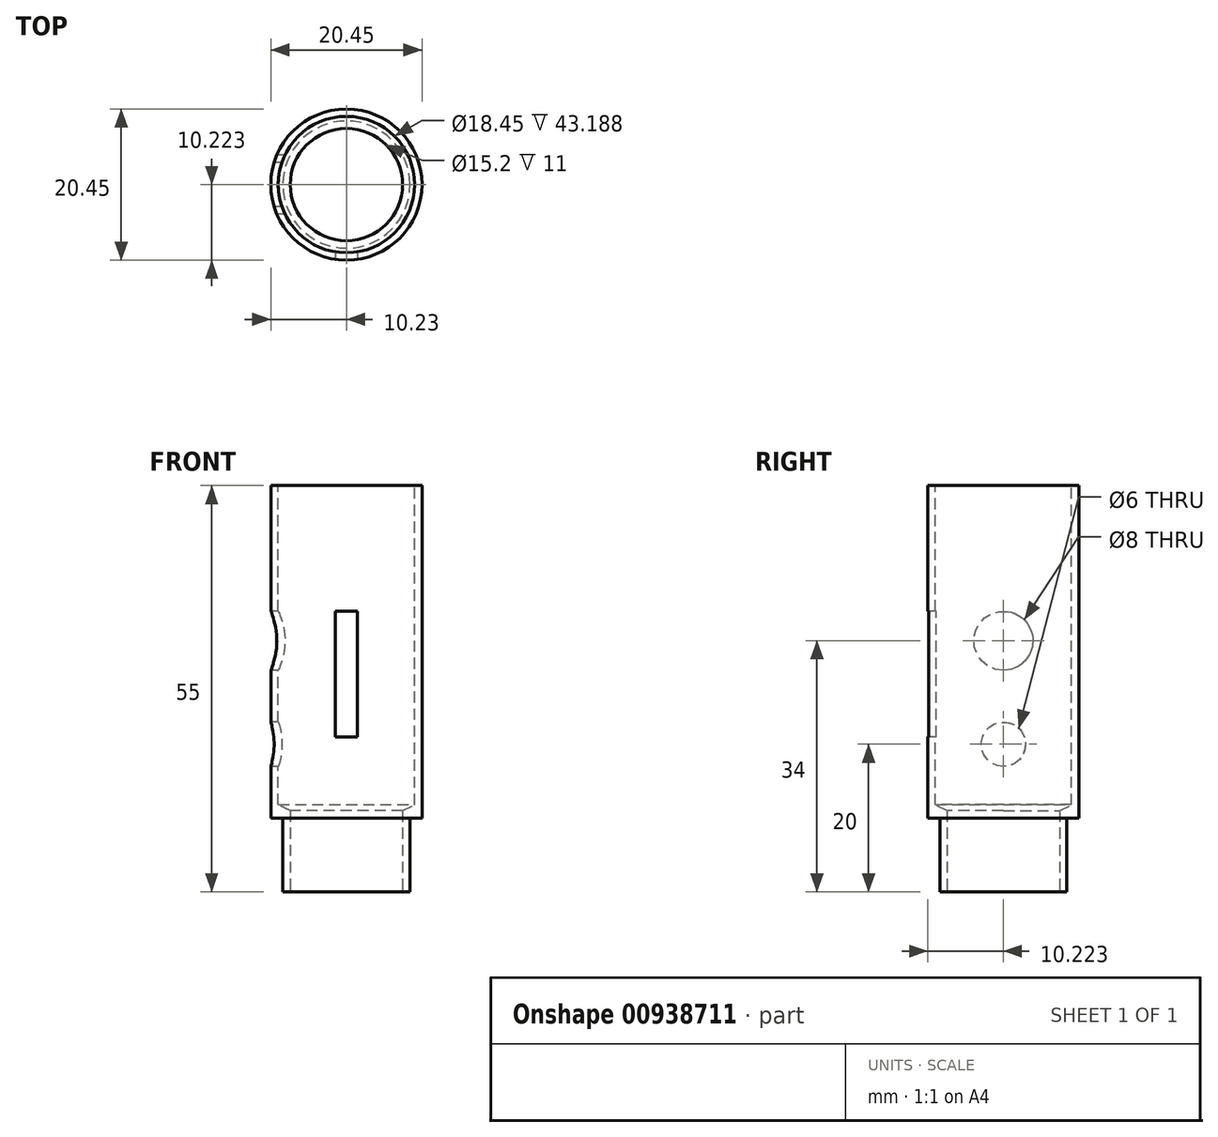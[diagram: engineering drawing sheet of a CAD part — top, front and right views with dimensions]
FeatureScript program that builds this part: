
annotation { "Feature Type Name" : "Feature", "Feature Type Description" : "" }
export const myFeature = defineFeature(function(context is Context, id is Id, definition is map)
    precondition{}
    {
        {
            var Q0;
            Q0=qCreatedBy(makeId("Top.planeOp"),FACE);
            var sketch = newSketch(context, id + "F0", { "sketchPlane" : qUnion([Q0])});
            skCircle(sketch, "E0", {"center": v(36.18, 39.19) * mm, "radius": 9.23 * mm});
            skCircle(sketch, "E1.0", {"center": v(36.18, 39.19) * mm, "radius": 10.23 * mm});
            skSolve(sketch);
        }
        {
            var Q0;
            Q0=qSketchRegion(id+"F0",true);
            extrude(context, id + "F1", {"entities" : qUnion([Q0]), "depth" : 45 * mm, "offsetDistance" : 25 * mm});
        }
        {
            var Q0;
            Q0=makeQuery(id+"F1.opExtrude","CAP_FACE",FACE,{"disambiguationData":[OSD([sQuery(id+"F0.wireOp",EDGE,"E0"),sQuery(id+"F0.wireOp",EDGE,"E1.0")])],"isStart":false});
            var sketch = newSketch(context, id + "F2", { "sketchPlane" : qUnion([Q0])});
            skCircle(sketch, "E2", {"center": v(36.18, 39.19) * mm, "radius": 7.6 * mm});
            skCircle(sketch, "E3", {"center": v(36.18, 39.19) * mm, "radius": 9.23 * mm});
            skSolve(sketch);
        }
        {
            var Q0;
            Q0=qSketchRegion(id+"F2",true);
            extrude(context, id + "F3", {"entities" : qUnion([Q0]), "operationType" : NewBodyOperationType.ADD, "oppositeDirection" : true, "depth" : 2 * mm, "offsetDistance" : 25 * mm});
        }
        {
            var Q0;
            Q0=makeQuery(id+"F3.opExtrude","CAP_EDGE",EDGE,{"disambiguationData":[OSD([sQuery(id+"F2.wireOp",EDGE,"E2")])],"isStart":false});
            chamfer(context, id + "F4", {"entities" : qUnion([Q0]), "chamferType" : ChamferType.TWO_OFFSETS, "width1" : 2 * mm, "oppositeDirection" : false, "width2" : 1 * mm, "tangentPropagation" : true});
        }
        {
            var Q0;
            Q0=makeQuery(id+"F3.boolean.opBoolean","MERGE",FACE,{"derivedFrom":[makeQuery(id+"F1.opExtrude","CAP_FACE",FACE,{"disambiguationData":[OSD([sQuery(id+"F0.wireOp",EDGE,"E0"),sQuery(id+"F0.wireOp",EDGE,"E1.0")])],"isStart":false}),makeQuery(id+"F3.opExtrude","CAP_FACE",FACE,{"disambiguationData":[OSD([sQuery(id+"F2.wireOp",EDGE,"E2"),sQuery(id+"F2.wireOp",EDGE,"E3")])],"isStart":true})]});
            var sketch = newSketch(context, id + "F5", { "sketchPlane" : qUnion([Q0])});
            skCircle(sketch, "E4", {"center": v(36.18, 39.19) * mm, "radius": 7.6 * mm});
            skCircle(sketch, "E5", {"center": v(36.18, 39.19) * mm, "radius": 8.6 * mm});
            skSolve(sketch);
        }
        {
            var Q0;
            Q0=qSketchRegion(id+"F5",true);
            extrude(context, id + "F6", {"entities" : qUnion([Q0]), "operationType" : NewBodyOperationType.ADD, "depth" : 10 * mm, "offsetDistance" : 25 * mm});
        }
        {
            var Q0;
            Q0=makeQuery(id+"F6.opExtrude","CAP_FACE",FACE,{"disambiguationData":[OSD([sQuery(id+"F5.wireOp",EDGE,"E4"),sQuery(id+"F5.wireOp",EDGE,"E5")])],"isStart":false});
            var sketch = newSketch(context, id + "F7", { "sketchPlane" : qUnion([Q0])});
            skCircle(sketch, "E6.0", {"center": v(36.18, 39.19) * mm, "radius": 8.6 * mm});
            skSolve(sketch);
        }
        {
            var Q0;
            Q0=qSketchRegion(id+"F7",true);
            extrude(context, id + "F8", {"entities" : qUnion([Q0]), "operationType" : NewBodyOperationType.ADD, "oppositeDirection" : true, "depth" : 2 * mm, "offsetDistance" : 25 * mm});
        }
        {
            var Q0;
            Q0=qCreatedBy(makeId("Front.planeOp"),FACE);
            cPlane(context, id + "F9", {"entities" : qUnion([Q0]), "cplaneType" : CPlaneType.OFFSET, "offset" : 40 * mm, "oppositeDirection" : true, "width" : 150 * mm, "height" : 150 * mm});
        }
        {
            var Q0;
            Q0=qCreatedBy(id+"F9.planeOp",FACE);
            var sketch = newSketch(context, id + "F10", { "sketchPlane" : qUnion([Q0])});
            skLineSegment(sketch, "E7.0", {"start": v(27.58, 55) * mm, "end": v(44.78, 55) * mm});
            skLineSegment(sketch, "E8.0", {"start": v(25.95, 0) * mm, "end": v(46.4, 0) * mm});
            skLineSegment(sketch, "E9", {"start": v(36.18, 55) * mm, "end": v(36.18, 0) * mm});
            skLineSegment(sketch, "E10", {"start": v(35.45, 27.5) * mm, "end": v(55.94, 27.5) * mm});
            skPoint(sketch, "E10.startSnap0", {"position": v(36.18, 27.5) * mm});
            skSolve(sketch);
        }
        {
            var Q0;
            Q0=makeQuery(id+"F1.opExtrude","SWEPT_BODY",BODY,{"disambiguationData":[OSD([sQuery(id+"F0.wireOp",EDGE,"E0"),sQuery(id+"F0.wireOp",EDGE,"E1.0")])]});
            var Q1;
            Q1=sQuery(id+"F10.wireOp",EDGE,"E10");
            transform(context, id + "F11", {"entities" : qUnion([Q0]), "transformType" : TransformType.ROTATION, "transformAxis" : qUnion([Q1]), "angle" : 180 * degree, "makeCopy" : false});
        }
        {
            var Q0;
            Q0=qCreatedBy(makeId("Top.planeOp"),FACE);
            var sketch = newSketch(context, id + "F12", { "sketchPlane" : qUnion([Q0])});
            skCircle(sketch, "E11.0", {"center": v(36.18, 40.81) * mm, "radius": 7.6 * mm});
            skSolve(sketch);
        }
        {
            var Q0;
            Q0 = qSketchRegion(id + "F12", true);
            extrude(context, id + "F13", {"entities" : qUnion([Q0]), "operationType" : NewBodyOperationType.REMOVE, "depth" : 25 * mm, "offsetDistance" : 25 * mm});
        }
        {
            var Q0;
            Q0=qCreatedBy(makeId("Right.planeOp"),FACE);
            var sketch = newSketch(context, id + "F14", { "sketchPlane" : qUnion([Q0])});
            skLineSegment(sketch, "E12.0", {"start": v(51.04, 55) * mm, "end": v(30.59, 55) * mm, "construction": true});
            skLineSegment(sketch, "E13", {"start": v(40.81, 55) * mm, "end": v(40.81, 9.9) * mm, "construction": true});
            skCircle(sketch, "E14", {"center": v(40.81, 34) * mm, "radius": 4 * mm});
            skCircle(sketch, "E15", {"center": v(40.81, 20) * mm, "radius": 3 * mm});
            skSolve(sketch);
        }
        {
            var Q0;
            Q0 = qSketchRegion(id + "F14", true);
            var Q1;
            Q1=makeQuery(id+"F1.opExtrude","SWEPT_FACE",FACE,{"disambiguationData":[OSD([sQuery(id+"F0.wireOp",EDGE,"E1.0")])]});
            extrude(context, id + "F15", {"entities" : qUnion([Q0]), "operationType" : NewBodyOperationType.REMOVE, "depth" : 35 * mm, "endBoundEntityFace" : qUnion([Q1]), "offsetDistance" : 25 * mm});
        }
        {
            var Q0;
            Q0=qCreatedBy(makeId("Front.planeOp"),FACE);
            var sketch = newSketch(context, id + "F16", { "sketchPlane" : qUnion([Q0])});
            skLineSegment(sketch, "E16.0", {"start": v(46.4, 55) * mm, "end": v(25.95, 55) * mm, "construction": true});
            skLineSegment(sketch, "E17", {"start": v(36.18, 55) * mm, "end": v(36.18, 24.81) * mm, "construction": true});
            skLineSegment(sketch, "E18.bottom", {"start": v(37.68, 38) * mm, "end": v(34.68, 38) * mm});
            skLineSegment(sketch, "E18.top", {"start": v(37.68, 21) * mm, "end": v(34.68, 21) * mm});
            skLineSegment(sketch, "E18.left", {"start": v(37.68, 38) * mm, "end": v(37.68, 21) * mm});
            skLineSegment(sketch, "E18.right", {"start": v(34.68, 38) * mm, "end": v(34.68, 21) * mm});
            skPoint(sketch, "E18.middle", {"position": v(36.18, 29.5) * mm});
            skSolve(sketch);
        }
        {
            var Q0;
            Q0 = qSketchRegion(id + "F16", true);
            extrude(context, id + "F17", {"entities" : qUnion([Q0]), "operationType" : NewBodyOperationType.REMOVE, "oppositeDirection" : true, "depth" : 35 * mm, "offsetDistance" : 25 * mm});
        }
    });
